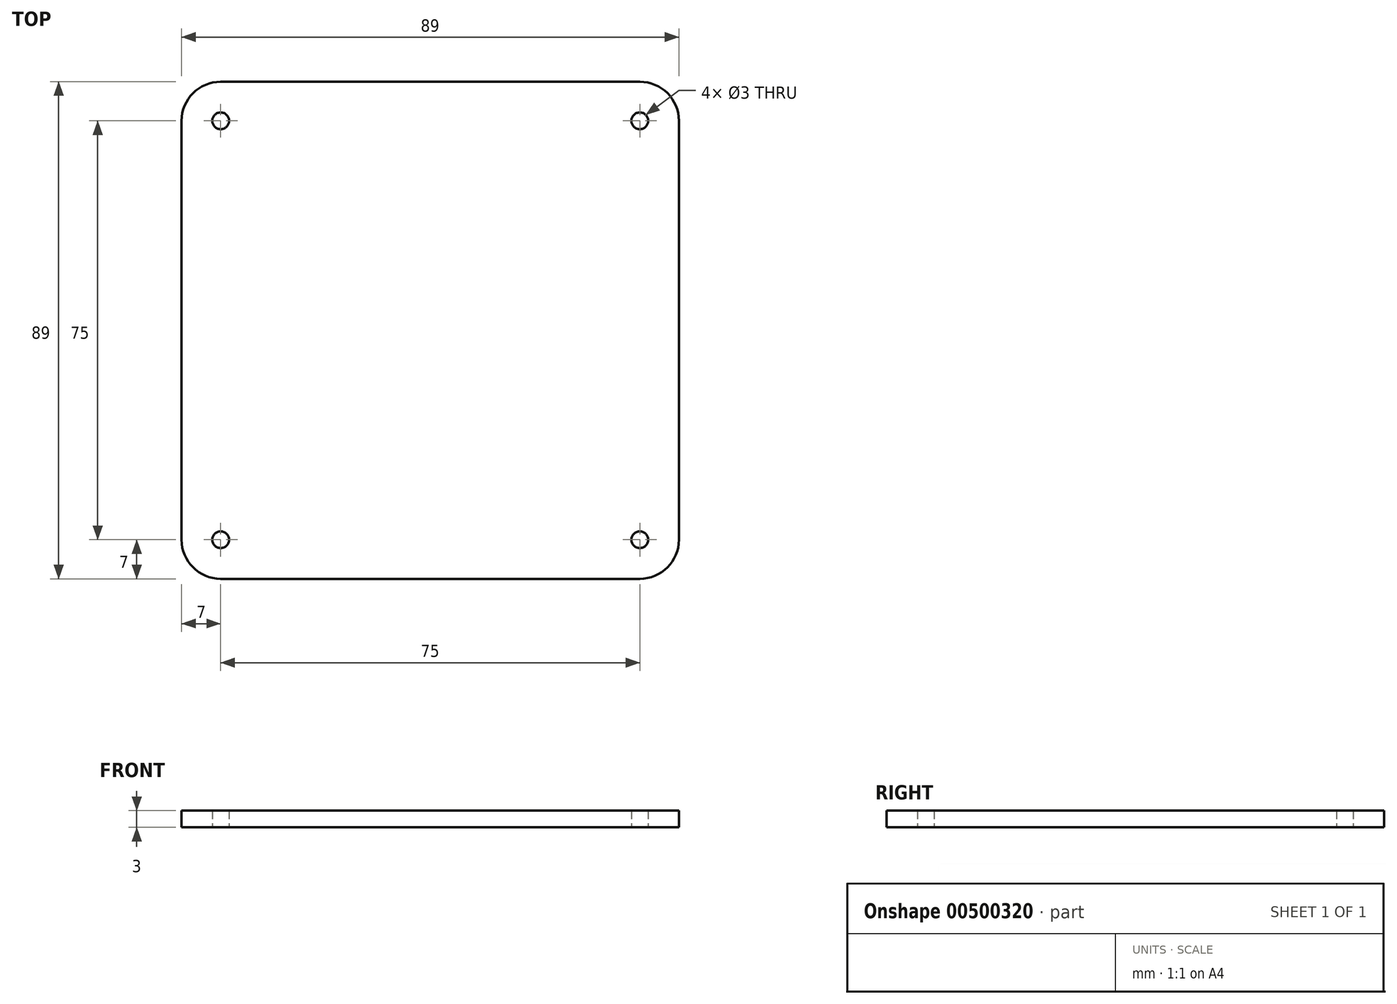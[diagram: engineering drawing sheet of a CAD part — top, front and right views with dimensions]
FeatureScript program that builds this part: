
annotation { "Feature Type Name" : "Feature", "Feature Type Description" : "" }
export const myFeature = defineFeature(function(context is Context, id is Id, definition is map)
    precondition{}
    {
        {
            var Q0;
            Q0=qCreatedBy(makeId("Top.planeOp"),FACE);
            var sketch = newSketch(context, id + "F0", { "sketchPlane" : qUnion([Q0])});
            skLineSegment(sketch, "E0.bottom", {"start": v(37.5, 37.5) * mm, "end": v(-37.5, 37.5) * mm});
            skLineSegment(sketch, "E0.top", {"start": v(37.5, -37.5) * mm, "end": v(-37.5, -37.5) * mm});
            skLineSegment(sketch, "E0.left", {"start": v(37.5, 37.5) * mm, "end": v(37.5, -37.5) * mm});
            skLineSegment(sketch, "E0.right", {"start": v(-37.5, 37.5) * mm, "end": v(-37.5, -37.5) * mm});
            skPoint(sketch, "E0.middle", {"position": v(0, 0) * mm});
            skLineSegment(sketch, "E1.bottom", {"start": v(44.5, 44.5) * mm, "end": v(-44.5, 44.5) * mm});
            skLineSegment(sketch, "E1.top", {"start": v(44.5, -44.5) * mm, "end": v(-44.5, -44.5) * mm});
            skLineSegment(sketch, "E1.left", {"start": v(44.5, 44.5) * mm, "end": v(44.5, -44.5) * mm});
            skLineSegment(sketch, "E1.right", {"start": v(-44.5, 44.5) * mm, "end": v(-44.5, -44.5) * mm});
            skCircle(sketch, "E2", {"center": v(37.5, 37.5) * mm, "radius": 7 * mm});
            skCircle(sketch, "E3", {"center": v(-37.5, 37.5) * mm, "radius": 7 * mm});
            skCircle(sketch, "E4", {"center": v(-37.5, -37.5) * mm, "radius": 7 * mm});
            skCircle(sketch, "E5", {"center": v(37.5, -37.5) * mm, "radius": 7 * mm});
            skCircle(sketch, "E6", {"center": v(-37.5, 37.5) * mm, "radius": 1.5 * mm});
            skCircle(sketch, "E7", {"center": v(37.5, 37.5) * mm, "radius": 1.5 * mm});
            skCircle(sketch, "E8", {"center": v(37.5, -37.5) * mm, "radius": 1.5 * mm});
            skCircle(sketch, "E9", {"center": v(-37.5, -37.5) * mm, "radius": 1.5 * mm});
            skSolve(sketch);
        }
        {
            var Q0;
            {var subQ0=sQuery(id+"F0.wireOp",EDGE,"E2");var subQ1=sQuery(id+"F0.wireOp",EDGE,"E0.bottom");var subQ2=makeQuery(id+"F0.imprint","INTERSECT",VERTEX,{"derivedFrom":[subQ1,subQ0]});Q0=makeQuery(id+"F0.imprint","IMPRINT",FACE,{"disambiguationData":[TD([[makeQuery(id+"F0.imprint","IMPRINT",EDGE,{"disambiguationData":[TD([[subQ2,-1.0]])],"derivedFrom":subQ1}),-1.0]])]});}
            var Q1;
            {var subQ0=sQuery(id+"F0.wireOp",EDGE,"E5");var subQ1=sQuery(id+"F0.wireOp",EDGE,"E0.top");var subQ2=makeQuery(id+"F0.imprint","INTERSECT",VERTEX,{"derivedFrom":[subQ1,subQ0]});Q1=makeQuery(id+"F0.imprint","IMPRINT",FACE,{"disambiguationData":[TD([[makeQuery(id+"F0.imprint","IMPRINT",EDGE,{"disambiguationData":[TD([[subQ2,-1.0]])],"derivedFrom":subQ1}),1.0]])]});}
            var Q2;
            {var subQ0=sQuery(id+"F0.wireOp",EDGE,"E2");var subQ1=sQuery(id+"F0.wireOp",EDGE,"E0.left");var subQ2=makeQuery(id+"F0.imprint","INTERSECT",VERTEX,{"derivedFrom":[subQ1,subQ0]});Q2=makeQuery(id+"F0.imprint","IMPRINT",FACE,{"disambiguationData":[TD([[makeQuery(id+"F0.imprint","IMPRINT",EDGE,{"disambiguationData":[TD([[subQ2,-1.0]])],"derivedFrom":subQ1}),1.0]])]});}
            var Q3;
            {var subQ0=sQuery(id+"F0.wireOp",EDGE,"E3");var subQ1=sQuery(id+"F0.wireOp",EDGE,"E0.right");var subQ2=makeQuery(id+"F0.imprint","INTERSECT",VERTEX,{"derivedFrom":[subQ1,subQ0]});Q3=makeQuery(id+"F0.imprint","IMPRINT",FACE,{"disambiguationData":[TD([[makeQuery(id+"F0.imprint","IMPRINT",EDGE,{"disambiguationData":[TD([[subQ2,-1.0]])],"derivedFrom":subQ1}),-1.0]])]});}
            var Q4;
            {var subQ2=sQuery(id+"F0.wireOp",EDGE,"E0.bottom");var subQ4=sQuery(id+"F0.wireOp",EDGE,"E7");var subQ9=makeQuery(id+"F0.imprint","INTERSECT",VERTEX,{"derivedFrom":[subQ2,subQ4]});Q4=makeQuery(id+"F0.imprint","IMPRINT",FACE,{"disambiguationData":[TD([[makeQuery(id+"F0.imprint","IMPRINT",EDGE,{"disambiguationData":[TD([[subQ9,-1.0]])],"derivedFrom":subQ2}),-1.0]])]});}
            var Q5;
            {var subQ0=sQuery(id+"F0.wireOp",EDGE,"E3");var subQ4=sQuery(id+"F0.wireOp",EDGE,"E0.bottom");var subQ8=makeQuery(id+"F0.imprint","INTERSECT",VERTEX,{"derivedFrom":[subQ4,subQ0]});Q5=makeQuery(id+"F0.imprint","IMPRINT",FACE,{"disambiguationData":[TD([[makeQuery(id+"F0.imprint","IMPRINT",EDGE,{"disambiguationData":[TD([[subQ8,-1.0]])],"derivedFrom":subQ4}),-1.0]])]});}
            var Q6;
            {var subQ4=sQuery(id+"F0.wireOp",EDGE,"E8");var subQ7=sQuery(id+"F0.wireOp",EDGE,"E0.top");var subQ9=makeQuery(id+"F0.imprint","INTERSECT",VERTEX,{"derivedFrom":[subQ7,subQ4]});Q6=makeQuery(id+"F0.imprint","IMPRINT",FACE,{"disambiguationData":[TD([[makeQuery(id+"F0.imprint","IMPRINT",EDGE,{"disambiguationData":[TD([[subQ9,-1.0]])],"derivedFrom":subQ7}),1.0]])]});}
            var Q7;
            {var subQ0=sQuery(id+"F0.wireOp",EDGE,"E4");var subQ5=sQuery(id+"F0.wireOp",EDGE,"E0.top");var subQ6=makeQuery(id+"F0.imprint","INTERSECT",VERTEX,{"derivedFrom":[subQ5,subQ0]});Q7=makeQuery(id+"F0.imprint","IMPRINT",FACE,{"disambiguationData":[TD([[makeQuery(id+"F0.imprint","IMPRINT",EDGE,{"disambiguationData":[TD([[subQ6,-1.0]])],"derivedFrom":subQ5}),1.0]])]});}
            var Q8;
            {var subQ5=sQuery(id+"F0.wireOp",EDGE,"E0.bottom");var subQ7=sQuery(id+"F0.wireOp",EDGE,"E2");var subQ12=makeQuery(id+"F0.imprint","INTERSECT",VERTEX,{"derivedFrom":[subQ5,subQ7]});Q8=makeQuery(id+"F0.imprint","IMPRINT",FACE,{"disambiguationData":[TD([[makeQuery(id+"F0.imprint","IMPRINT",EDGE,{"disambiguationData":[TD([[subQ12,-1.0]])],"derivedFrom":subQ5}),1.0]])]});}
            var Q9;
            {var subQ0=sQuery(id+"F0.wireOp",EDGE,"E3");var subQ1=sQuery(id+"F0.wireOp",EDGE,"E0.bottom");var subQ2=makeQuery(id+"F0.imprint","INTERSECT",VERTEX,{"derivedFrom":[subQ1,subQ0]});Q9=makeQuery(id+"F0.imprint","IMPRINT",FACE,{"disambiguationData":[TD([[makeQuery(id+"F0.imprint","IMPRINT",EDGE,{"disambiguationData":[TD([[subQ2,-1.0]])],"derivedFrom":subQ1}),1.0]])]});}
            var Q10;
            {var subQ0=sQuery(id+"F0.wireOp",EDGE,"E7");var subQ1=sQuery(id+"F0.wireOp",EDGE,"E0.bottom");var subQ2=makeQuery(id+"F0.imprint","INTERSECT",VERTEX,{"derivedFrom":[subQ1,subQ0]});Q10=makeQuery(id+"F0.imprint","IMPRINT",FACE,{"disambiguationData":[TD([[makeQuery(id+"F0.imprint","IMPRINT",EDGE,{"disambiguationData":[TD([[subQ2,-1.0]])],"derivedFrom":subQ1}),1.0]])]});}
            var Q11;
            {var subQ0=sQuery(id+"F0.wireOp",EDGE,"E8");var subQ1=sQuery(id+"F0.wireOp",EDGE,"E0.top");var subQ2=makeQuery(id+"F0.imprint","INTERSECT",VERTEX,{"derivedFrom":[subQ1,subQ0]});Q11=makeQuery(id+"F0.imprint","IMPRINT",FACE,{"disambiguationData":[TD([[makeQuery(id+"F0.imprint","IMPRINT",EDGE,{"disambiguationData":[TD([[subQ2,-1.0]])],"derivedFrom":subQ1}),-1.0]])]});}
            var Q12;
            {var subQ0=sQuery(id+"F0.wireOp",EDGE,"E4");var subQ1=sQuery(id+"F0.wireOp",EDGE,"E0.top");var subQ2=makeQuery(id+"F0.imprint","INTERSECT",VERTEX,{"derivedFrom":[subQ1,subQ0]});Q12=makeQuery(id+"F0.imprint","IMPRINT",FACE,{"disambiguationData":[TD([[makeQuery(id+"F0.imprint","IMPRINT",EDGE,{"disambiguationData":[TD([[subQ2,-1.0]])],"derivedFrom":subQ1}),-1.0]])]});}
            extrude(context, id + "F1", {"entities" : qUnion([Q0, Q1, Q2, Q3, Q4, Q5, Q6, Q7, Q8, Q9, Q10, Q11, Q12]), "depth" : 3 * mm});
        }
    });
